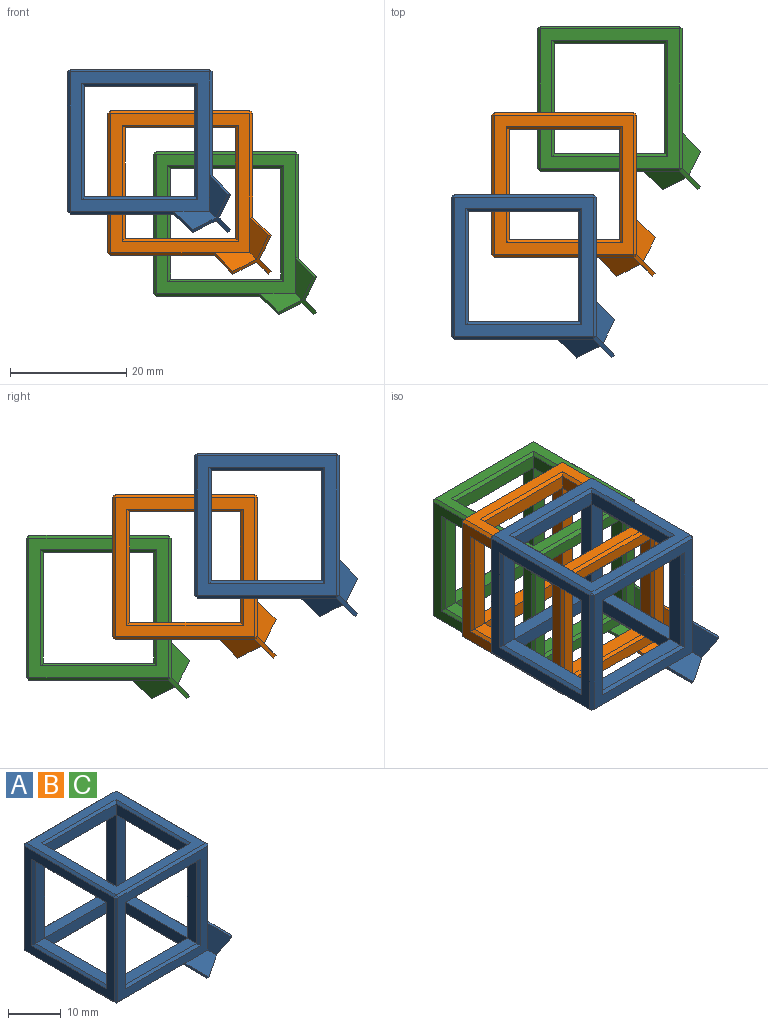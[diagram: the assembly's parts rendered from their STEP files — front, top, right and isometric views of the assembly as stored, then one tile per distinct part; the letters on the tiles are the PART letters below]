
ASSEMBLY  parts=3 mates=2
PART A: 83 faces, bbox 28.2x28.2x28.2 mm
  f0: plane 17.88x0.5mm, normal (0.71,-0.71,0), area 12.6mm2, adj f13,f18,f41,f73
  f1: plane 17.88x0.5mm, normal (0.71,0,-0.71), area 12.6mm2, adj f13,f16,f48,f79
  f2: plane 19x2.5mm, normal (0,0,1), area 47.5mm2, adj f8,f9,f27,f58
  f3: plane 19x2.5mm, normal (0,0,1), area 47.5mm2, adj f22,f23,f26,f37
  f4: plane 19x2.5mm, normal (0,0,1), area 47.5mm2, adj f11,f17,f25,f62
  f5: plane 19x2.5mm, normal (0,0,-1), area 47.5mm2, adj f8,f9,f28,f59
  f6: plane 19x2.5mm, normal (0,0,-1), area 47.5mm2, adj f22,f23,f29,f38
  f7: plane 19x2.5mm, normal (0,0,-1), area 47.5mm2, adj f11,f17,f30,f63
  f8: plane 19x2.5mm, normal (1,0,0), area 47.5mm2, adj f2,f5,f22,f60
  f9: plane 19x2.5mm, normal (-1,0,0), area 47.5mm2, adj f2,f5,f20,f57
  f10: plane 19x2.5mm, normal (0,0,1), area 47.5mm2, adj f20,f21,f24,f70
  f11: plane 19x2.5mm, normal (1,0,0), area 47.5mm2, adj f4,f7,f23,f64
  f12: plane 19x2.5mm, normal (0,0,-1), area 47.5mm2, adj f20,f21,f31,f71
  f13: plane 24x24mm, normal (1,0,0), area 176mm2, adj f0,f1,f40,f44,f69,f70,f71,f72
  f14: plane 24x24mm, normal (0,0,1), area 176mm2, adj f40,f43,f45,f46,f65,f66,f67,f68
  f15: plane 24x24mm, normal (-1,0,0), area 176mm2, adj f36,f37,f38,f39,f46,f50,f53,f56
  f16: plane 24x24mm, normal (0,0,-1), area 176mm2, adj f1,f32,f33,f34,f35,f51,f52,f56
  f17: plane 19x2.5mm, normal (-1,0,0), area 47.5mm2, adj f4,f7,f21,f61
  f18: plane 24x24mm, normal (0,-1,0), area 176mm2, adj f0,f43,f50,f51,f61,f62,f63,f64
  f19: plane 24x24mm, normal (0,1,0), area 176mm2, adj f44,f45,f52,f53,f57,f58,f59,f60
  f20: plane 19x2.5mm, normal (0,-1,0), area 47.5mm2, adj f9,f10,f12,f69
  f21: plane 19x2.5mm, normal (0,1,0), area 47.5mm2, adj f10,f12,f17,f72
  f22: plane 19x2.5mm, normal (0,-1,0), area 47.5mm2, adj f3,f6,f8,f36
  f23: plane 19x2.5mm, normal (0,1,0), area 47.5mm2, adj f3,f6,f11,f39
  f24: plane 19x2.5mm, normal (-1,0,0), area 47.5mm2, adj f10,f25,f27,f32
  f25: plane 19x2.5mm, normal (0,1,0), area 47.5mm2, adj f4,f24,f26,f33
  f26: plane 19x2.5mm, normal (1,0,0), area 47.5mm2, adj f3,f25,f27,f35
  f27: plane 19x2.5mm, normal (0,-1,0), area 47.5mm2, adj f2,f24,f26,f34
  f28: plane 19x2.5mm, normal (0,-1,0), area 47.5mm2, adj f5,f29,f31,f67
  f29: plane 19x2.5mm, normal (1,0,0), area 47.5mm2, adj f6,f28,f30,f68
  f30: plane 19x2.5mm, normal (0,1,0), area 47.5mm2, adj f7,f29,f31,f66
  f31: plane 19x2.5mm, normal (-1,0,0), area 47.5mm2, adj f12,f28,f30,f65
  f32: plane 20x0.5mm, normal (-0.71,0,-0.71), area 13.8mm2, adj f16,f24,f33,f34
  f33: plane 20x0.5mm, normal (0,0.71,-0.71), area 13.8mm2, adj f16,f25,f32,f35
  f34: plane 20x0.5mm, normal (0,-0.71,-0.71), area 13.8mm2, adj f16,f27,f32,f35
  f35: plane 20x0.5mm, normal (0.71,0,-0.71), area 13.8mm2, adj f16,f26,f33,f34
  f36: plane 20x0.5mm, normal (-0.71,-0.71,0), area 13.8mm2, adj f15,f22,f37,f38
  f37: plane 20x0.5mm, normal (-0.71,0,0.71), area 13.8mm2, adj f3,f15,f36,f39
  f38: plane 20x0.5mm, normal (-0.71,0,-0.71), area 13.8mm2, adj f6,f15,f36,f39
  f39: plane 20x0.5mm, normal (-0.71,0.71,0), area 13.8mm2, adj f15,f23,f37,f38
  f40: plane 24x0.5mm, normal (0.71,0,0.71), area 17mm2, adj f13,f14,f41,f42
  f41: plane 0.5x0.5mm, normal (0.58,-0.58,0.58), area 0.2mm2, adj f0,f40,f43
  f42: plane 0.5x0.5mm, normal (0.58,0.58,0.58), area 0.2mm2, adj f40,f44,f45
  f43: plane 24x0.5mm, normal (0,-0.71,0.71), area 17mm2, adj f14,f18,f41,f47
  f44: plane 24x0.5mm, normal (0.71,0.71,0), area 17mm2, adj f13,f19,f42,f48
  f45: plane 24x0.5mm, normal (0,0.71,0.71), area 17mm2, adj f14,f19,f42,f49
  f46: plane 24x0.5mm, normal (-0.71,0,0.71), area 17mm2, adj f14,f15,f47,f49
  f47: plane 0.5x0.5mm, normal (-0.58,-0.58,0.58), area 0.2mm2, adj f43,f46,f50
  f48: plane 0.5x0.5mm, normal (0.58,0.58,-0.58), area 0.2mm2, adj f1,f44,f52
  f49: plane 0.5x0.5mm, normal (-0.58,0.58,0.58), area 0.2mm2, adj f45,f46,f53
  f50: plane 24x0.5mm, normal (-0.71,-0.71,0), area 17mm2, adj f15,f18,f47,f54
  f51: plane 17.88x0.5mm, normal (0,-0.71,-0.71), area 12.6mm2, adj f16,f18,f54,f76
  f52: plane 24x0.5mm, normal (0,0.71,-0.71), area 17mm2, adj f16,f19,f48,f55
  f53: plane 24x0.5mm, normal (-0.71,0.71,0), area 17mm2, adj f15,f19,f49,f55
  f54: plane 0.5x0.5mm, normal (-0.58,-0.58,-0.58), area 0.2mm2, adj f50,f51,f56
  f55: plane 0.5x0.5mm, normal (-0.58,0.58,-0.58), area 0.2mm2, adj f52,f53,f56
  f56: plane 24x0.5mm, normal (-0.71,0,-0.71), area 17mm2, adj f15,f16,f54,f55
  f57: plane 20x0.5mm, normal (-0.71,0.71,0), area 13.8mm2, adj f9,f19,f58,f59
  f58: plane 20x0.5mm, normal (0,0.71,0.71), area 13.8mm2, adj f2,f19,f57,f60
  f59: plane 20x0.5mm, normal (0,0.71,-0.71), area 13.8mm2, adj f5,f19,f57,f60
  f60: plane 20x0.5mm, normal (0.71,0.71,0), area 13.8mm2, adj f8,f19,f58,f59
  f61: plane 20x0.5mm, normal (-0.71,-0.71,0), area 13.8mm2, adj f17,f18,f62,f63
  f62: plane 20x0.5mm, normal (0,-0.71,0.71), area 13.8mm2, adj f4,f18,f61,f64
  f63: plane 20x0.5mm, normal (0,-0.71,-0.71), area 13.8mm2, adj f7,f18,f61,f64
  f64: plane 20x0.5mm, normal (0.71,-0.71,0), area 13.8mm2, adj f11,f18,f62,f63
  f65: plane 20x0.5mm, normal (-0.71,0,0.71), area 13.8mm2, adj f14,f31,f66,f67
  f66: plane 20x0.5mm, normal (0,0.71,0.71), area 13.8mm2, adj f14,f30,f65,f68
  f67: plane 20x0.5mm, normal (0,-0.71,0.71), area 13.8mm2, adj f14,f28,f65,f68
  f68: plane 20x0.5mm, normal (0.71,0,0.71), area 13.8mm2, adj f14,f29,f66,f67
  f69: plane 20x0.5mm, normal (0.71,-0.71,0), area 13.8mm2, adj f13,f20,f70,f71
  f70: plane 20x0.5mm, normal (0.71,0,0.71), area 13.8mm2, adj f10,f13,f69,f72
  f71: plane 20x0.5mm, normal (0.71,0,-0.71), area 13.8mm2, adj f12,f13,f69,f72
  f72: plane 20x0.5mm, normal (0.71,0.71,0), area 13.8mm2, adj f13,f21,f70,f71
  f73: plane 3.7x3.7mm, normal (0.41,-0.41,0.82), area 3.9mm2, adj f0,f74,f80,f81
  f74: plane 7.28x3.2mm, normal (-0.71,-0.71,0), area 18.8mm2, adj f18,f73,f75,f80
  f75: plane 7.28x3.2mm, normal (0,-0.71,0.71), area 18.8mm2, adj f18,f74,f76,f80
  f76: plane 3.7x3.7mm, normal (-0.82,-0.41,-0.41), area 3.9mm2, adj f51,f75,f77,f80
  f77: plane 7.28x3.2mm, normal (0,0.71,-0.71), area 18.8mm2, adj f16,f76,f78,f80
  f78: plane 7.28x3.2mm, normal (-0.71,0,-0.71), area 18.8mm2, adj f16,f77,f79,f80
  f79: plane 3.7x3.7mm, normal (0.41,0.82,-0.41), area 3.9mm2, adj f1,f78,f80,f82
  f80: plane 6.62x6.62mm, normal (0.58,-0.58,-0.58), area 10.8mm2, adj f73,f74,f75,f76,f77,f78,f79,f81
  f81: plane 7.28x3.2mm, normal (0.71,0.71,0), area 18.8mm2, adj f13,f73,f80,f82
  f82: plane 7.28x3.2mm, normal (0.71,0,0.71), area 18.8mm2, adj f13,f79,f80,f81
PART B: same geometry as A
PART C: same geometry as A
PLACE A t=(-0.12,-1.27,-3.46)mm
PLACE B rot(axis=(1,0,0),0deg) t=(6.84,12.84,-10.61)mm fixed
PLACE C t=(14.69,27.73,-17.65)mm
MATE planar C.f80 <-> B.f80  axis (0.58,-0.58,-0.58) through (28.01,14.41,-30.97)mm
MATE planar B.f80 <-> A.f80  axis (0.58,-0.58,-0.58) through (20.16,-0.48,-23.93)mm
